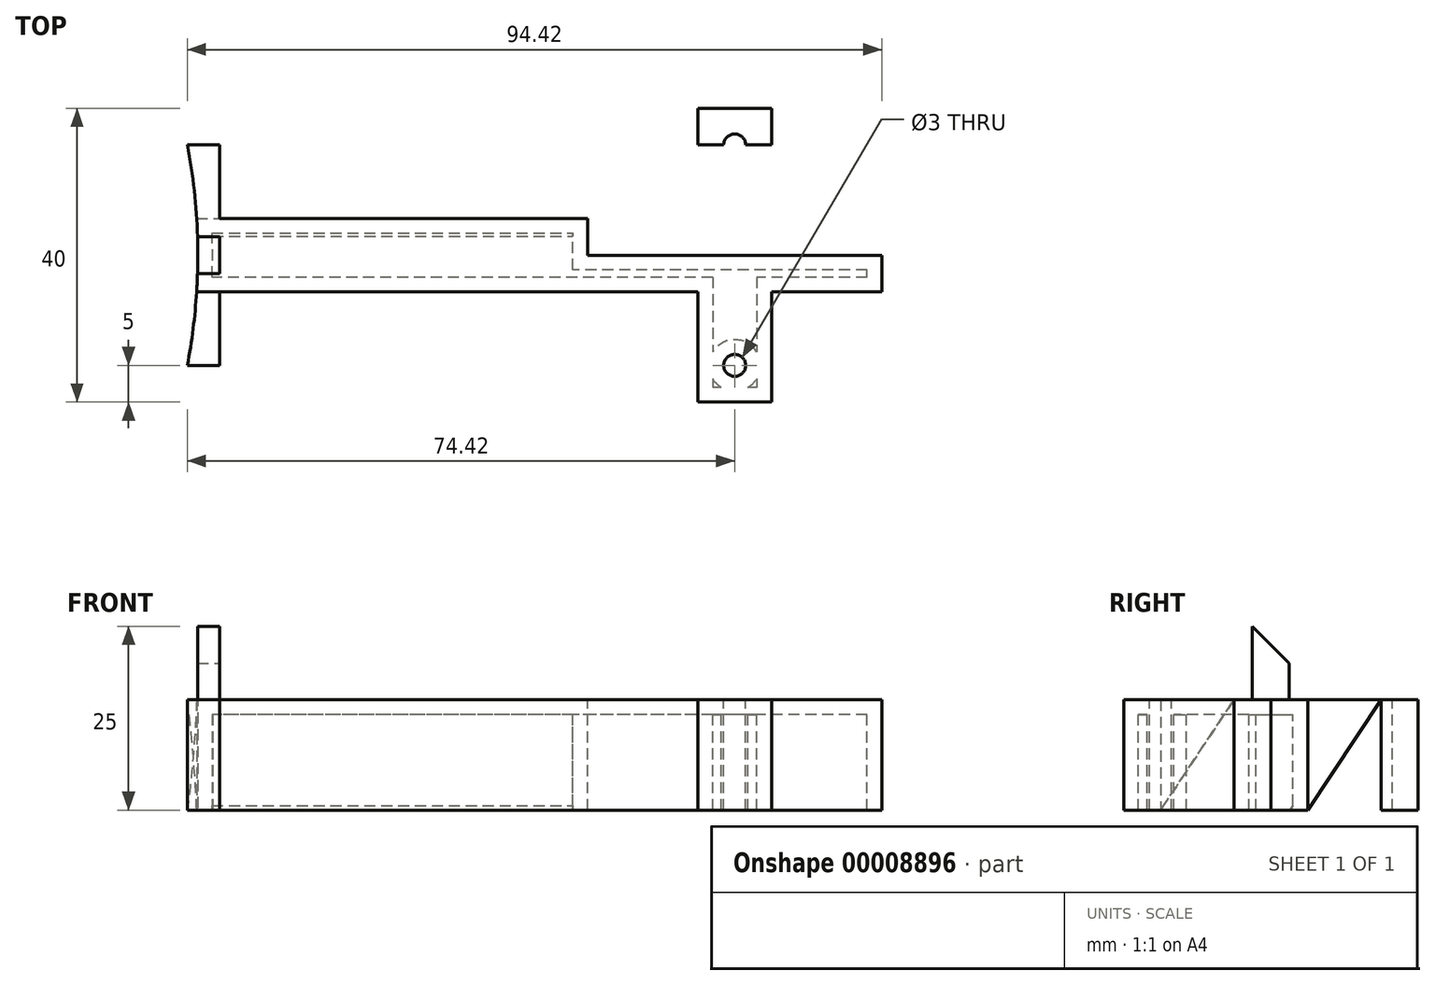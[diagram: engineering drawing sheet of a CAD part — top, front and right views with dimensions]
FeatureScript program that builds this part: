
annotation { "Feature Type Name" : "Feature", "Feature Type Description" : "" }
export const myFeature = defineFeature(function(context is Context, id is Id, definition is map)
    precondition{}
    {
        {
            var Q0;
            Q0=qCreatedBy(makeId("Top.planeOp"),FACE);
            var sketch = newSketch(context, id + "F0", { "sketchPlane" : qUnion([Q0])});
            skArc(sketch, "E0", {"start": v(78.58, -15) * mm, "mid": v(80, 0) * mm, "end": v(78.58, 15) * mm});
            skArc(sketch, "E1.0", {"start": v(81.63, -15) * mm, "mid": v(83, 0) * mm, "end": v(81.63, 15) * mm});
            skLineSegment(sketch, "E2", {"start": v(80, 0) * mm, "end": v(83, 0) * mm, "construction": true});
            skLineSegment(sketch, "E3.0", {"start": v(79.84, -5) * mm, "end": v(83, -5) * mm, "construction": true});
            skLineSegment(sketch, "E4.0", {"start": v(79.84, 5) * mm, "end": v(83, 5) * mm, "construction": true});
            skLineSegment(sketch, "E5", {"start": v(83, 0) * mm, "end": v(83, 15) * mm});
            skLineSegment(sketch, "E6", {"start": v(83, 0) * mm, "end": v(83, -15) * mm});
            skLineSegment(sketch, "E7", {"start": v(83, 15) * mm, "end": v(78.58, 15) * mm});
            skLineSegment(sketch, "E8", {"start": v(83, -15) * mm, "end": v(78.58, -15) * mm});
            skSolve(sketch);
        }
        {
            var Q0;
            {var subQ3=sQuery(id+"F0.wireOp",EDGE,"E0");Q0=makeQuery(id+"F0.imprint","IMPRINT",FACE,{"disambiguationData":[TD([[makeQuery(id+"F0.imprint","IMPRINT",EDGE,{"derivedFrom":subQ3}),-1.0]])]});}
            var Q1;
            {var subQ1=sQuery(id+"F0.wireOp",EDGE,"E5");Q1=makeQuery(id+"F0.imprint","IMPRINT",FACE,{"disambiguationData":[TD([[makeQuery(id+"F0.imprint","IMPRINT",EDGE,{"derivedFrom":subQ1}),1.0]])]});}
            var Q2;
            {var subQ1=sQuery(id+"F0.wireOp",EDGE,"E6");Q2=makeQuery(id+"F0.imprint","IMPRINT",FACE,{"disambiguationData":[TD([[makeQuery(id+"F0.imprint","IMPRINT",EDGE,{"derivedFrom":subQ1}),-1.0]])]});}
            extrude(context, id + "F1", {"entities" : qUnion([Q0, Q1, Q2]), "depth" : 15 * mm});
        }
        {
            var Q0;
            Q0=makeQuery(id+"F1.opExtrude","SWEPT_FACE",FACE,{"disambiguationData":[OSD([sQuery(id+"F0.wireOp",EDGE,"E5"),sQuery(id+"F0.wireOp",EDGE,"E6")])]});
            var sketch = newSketch(context, id + "F2", { "sketchPlane" : qUnion([Q0])});
            skLineSegment(sketch, "E9.0", {"start": v(-15, 10) * mm, "end": v(15, 10) * mm});
            skLineSegment(sketch, "E10", {"start": v(0, 10) * mm, "end": v(0, 15) * mm});
            skLineSegment(sketch, "E11.0", {"start": v(5, 0) * mm, "end": v(5, 15) * mm});
            skLineSegment(sketch, "E12.0", {"start": v(-5, 0) * mm, "end": v(-5, 15) * mm});
            skLineSegment(sketch, "E13", {"start": v(15, 0) * mm, "end": v(-15, 0) * mm});
            skLineSegment(sketch, "E14", {"start": v(15, 15) * mm, "end": v(-15, 15) * mm});
            skSolve(sketch);
        }
        {
            var Q0;
            {var subQ2=sQuery(id+"F2.wireOp",EDGE,"E10");Q0=makeQuery(id+"F2.imprint","IMPRINT",FACE,{"disambiguationData":[TD([[makeQuery(id+"F2.imprint","IMPRINT",EDGE,{"derivedFrom":subQ2}),-1.0]])]});}
            var Q1;
            {var subQ2=sQuery(id+"F2.wireOp",EDGE,"E10");Q1=makeQuery(id+"F2.imprint","IMPRINT",FACE,{"disambiguationData":[TD([[makeQuery(id+"F2.imprint","IMPRINT",EDGE,{"derivedFrom":subQ2}),1.0]])]});}
            var Q2;
            {var subQ5=sQuery(id+"F2.wireOp",EDGE,"E9.0");var subQ8=makeQuery(id+"F2.imprint","INTERSECT",VERTEX,{"derivedFrom":[subQ5,sQuery(id+"F2.wireOp",EDGE,"E10")]});Q2=makeQuery(id+"F2.imprint","IMPRINT",FACE,{"disambiguationData":[TD([[makeQuery(id+"F2.imprint","IMPRINT",EDGE,{"disambiguationData":[TD([[subQ8,1.0]])],"derivedFrom":subQ5}),-1.0]])]});}
            extrude(context, id + "F3", {"entities" : qUnion([Q0, Q1, Q2]), "operationType" : NewBodyOperationType.ADD, "depth" : 90 * mm});
        }
        {
            var Q0;
            Q0=makeQuery(id+"F3.boolean.opBoolean","MERGE",FACE,{"derivedFrom":[makeQuery(id+"F1.opExtrude","CAP_FACE",FACE,{"disambiguationData":[OSD([sQuery(id+"F0.wireOp",EDGE,"E0"),sQuery(id+"F0.wireOp",EDGE,"E5"),sQuery(id+"F0.wireOp",EDGE,"E6"),sQuery(id+"F0.wireOp",EDGE,"E7"),sQuery(id+"F0.wireOp",EDGE,"E8")])],"isStart":false}),makeQuery(id+"F3.opExtrude","SWEPT_FACE",FACE,{"disambiguationData":[OSD([sQuery(id+"F2.wireOp",EDGE,"E14")])]})]});
            var sketch = newSketch(context, id + "F4", { "sketchPlane" : qUnion([Q0])});
            skLineSegment(sketch, "E15.0", {"start": v(133, -5) * mm, "end": v(133, 5) * mm});
            skLineSegment(sketch, "E16.0", {"start": v(138, -5) * mm, "end": v(138, 5) * mm});
            skLineSegment(sketch, "E17.0", {"start": v(168, -5) * mm, "end": v(168, 5) * mm});
            skLineSegment(sketch, "E18", {"start": v(168, -5) * mm, "end": v(133, -5) * mm});
            skLineSegment(sketch, "E19.0", {"start": v(173, 0) * mm, "end": v(83, 0) * mm});
            skCircle(sketch, "E20", {"center": v(168, 0) * mm, "radius": 1.5 * mm});
            skCircle(sketch, "E21", {"center": v(138, 0) * mm, "radius": 1.5 * mm});
            skSolve(sketch);
        }
        {
            var Q0;
            {var subQ0=sQuery(id+"F4.wireOp",EDGE,"E20");var subQ3=sQuery(id+"F4.wireOp",EDGE,"E17.0");var subQ4=makeQuery(id+"F4.imprint","INTERSECT",VERTEX,{"disambiguationData":[OD(0.0)],"derivedFrom":[subQ3,subQ0]});Q0=makeQuery(id+"F4.imprint","IMPRINT",FACE,{"disambiguationData":[TD([[makeQuery(id+"F4.imprint","IMPRINT",EDGE,{"disambiguationData":[TD([[subQ4,-1.0]])],"derivedFrom":subQ3}),1.0]])]});}
            var Q1;
            {var subQ0=sQuery(id+"F4.wireOp",EDGE,"E20");var subQ3=sQuery(id+"F4.wireOp",EDGE,"E17.0");var subQ4=makeQuery(id+"F4.imprint","INTERSECT",VERTEX,{"disambiguationData":[OD(0.0)],"derivedFrom":[subQ3,subQ0]});Q1=makeQuery(id+"F4.imprint","IMPRINT",FACE,{"disambiguationData":[TD([[makeQuery(id+"F4.imprint","IMPRINT",EDGE,{"disambiguationData":[TD([[subQ4,-1.0]])],"derivedFrom":subQ3}),-1.0]])]});}
            var Q2;
            {var subQ1=sQuery(id+"F4.wireOp",EDGE,"E19.0");var subQ3=sQuery(id+"F4.wireOp",EDGE,"E17.0");var subQ5=makeQuery(id+"F4.imprint","INTERSECT",VERTEX,{"derivedFrom":[subQ3,subQ1]});Q2=makeQuery(id+"F4.imprint","IMPRINT",FACE,{"disambiguationData":[TD([[makeQuery(id+"F4.imprint","IMPRINT",EDGE,{"disambiguationData":[TD([[subQ5,-1.0]])],"derivedFrom":subQ3}),1.0]])]});}
            var Q3;
            {var subQ1=sQuery(id+"F4.wireOp",EDGE,"E19.0");var subQ3=sQuery(id+"F4.wireOp",EDGE,"E17.0");var subQ5=makeQuery(id+"F4.imprint","INTERSECT",VERTEX,{"derivedFrom":[subQ3,subQ1]});Q3=makeQuery(id+"F4.imprint","IMPRINT",FACE,{"disambiguationData":[TD([[makeQuery(id+"F4.imprint","IMPRINT",EDGE,{"disambiguationData":[TD([[subQ5,-1.0]])],"derivedFrom":subQ3}),-1.0]])]});}
            var Q4;
            {var subQ0=sQuery(id+"F4.wireOp",EDGE,"E21");var subQ3=sQuery(id+"F4.wireOp",EDGE,"E16.0");var subQ4=makeQuery(id+"F4.imprint","INTERSECT",VERTEX,{"disambiguationData":[OD(0.0)],"derivedFrom":[subQ3,subQ0]});Q4=makeQuery(id+"F4.imprint","IMPRINT",FACE,{"disambiguationData":[TD([[makeQuery(id+"F4.imprint","IMPRINT",EDGE,{"disambiguationData":[TD([[subQ4,-1.0]])],"derivedFrom":subQ3}),1.0]])]});}
            var Q5;
            {var subQ1=sQuery(id+"F4.wireOp",EDGE,"E19.0");var subQ3=sQuery(id+"F4.wireOp",EDGE,"E16.0");var subQ5=makeQuery(id+"F4.imprint","INTERSECT",VERTEX,{"derivedFrom":[subQ3,subQ1]});Q5=makeQuery(id+"F4.imprint","IMPRINT",FACE,{"disambiguationData":[TD([[makeQuery(id+"F4.imprint","IMPRINT",EDGE,{"disambiguationData":[TD([[subQ5,-1.0]])],"derivedFrom":subQ3}),1.0]])]});}
            var Q6;
            {var subQ1=sQuery(id+"F4.wireOp",EDGE,"E19.0");var subQ3=sQuery(id+"F4.wireOp",EDGE,"E16.0");var subQ5=makeQuery(id+"F4.imprint","INTERSECT",VERTEX,{"derivedFrom":[subQ3,subQ1]});Q6=makeQuery(id+"F4.imprint","IMPRINT",FACE,{"disambiguationData":[TD([[makeQuery(id+"F4.imprint","IMPRINT",EDGE,{"disambiguationData":[TD([[subQ5,-1.0]])],"derivedFrom":subQ3}),-1.0]])]});}
            var Q7;
            {var subQ1=sQuery(id+"F4.wireOp",EDGE,"E21");var subQ3=sQuery(id+"F4.wireOp",EDGE,"E16.0");var subQ5=makeQuery(id+"F4.imprint","INTERSECT",VERTEX,{"disambiguationData":[OD(0.0)],"derivedFrom":[subQ3,subQ1]});Q7=makeQuery(id+"F4.imprint","IMPRINT",FACE,{"disambiguationData":[TD([[makeQuery(id+"F4.imprint","IMPRINT",EDGE,{"disambiguationData":[TD([[subQ5,-1.0]])],"derivedFrom":subQ3}),-1.0]])]});}
            extrude(context, id + "F5", {"entities" : qUnion([Q0, Q1, Q2, Q3, Q4, Q5, Q6, Q7]), "operationType" : NewBodyOperationType.REMOVE, "oppositeDirection" : true, "depth" : 25 * mm});
        }
        {
            var Q0;
            Q0=makeQuery(id+"F3.boolean.opBoolean","MERGE",FACE,{"derivedFrom":[makeQuery(id+"F1.opExtrude","CAP_FACE",FACE,{"disambiguationData":[OSD([sQuery(id+"F0.wireOp",EDGE,"E0"),sQuery(id+"F0.wireOp",EDGE,"E5"),sQuery(id+"F0.wireOp",EDGE,"E6"),sQuery(id+"F0.wireOp",EDGE,"E7"),sQuery(id+"F0.wireOp",EDGE,"E8")])],"isStart":false}),makeQuery(id+"F3.opExtrude","SWEPT_FACE",FACE,{"disambiguationData":[OSD([sQuery(id+"F2.wireOp",EDGE,"E14")])]})]});
            var sketch = newSketch(context, id + "F6", { "sketchPlane" : qUnion([Q0])});
            skLineSegment(sketch, "E22.0", {"start": v(153, -5) * mm, "end": v(153, 5) * mm});
            skLineSegment(sketch, "E23", {"start": v(153, 5) * mm, "end": v(153, 20) * mm});
            skLineSegment(sketch, "E24", {"start": v(153, -5) * mm, "end": v(153, -20) * mm});
            skLineSegment(sketch, "E25.0", {"start": v(158, 5) * mm, "end": v(158, 20) * mm});
            skLineSegment(sketch, "E26.0", {"start": v(148, 5) * mm, "end": v(148, 20) * mm});
            skLineSegment(sketch, "E27.0", {"start": v(148, -5) * mm, "end": v(148, -20) * mm});
            skLineSegment(sketch, "E28.0", {"start": v(158, -5) * mm, "end": v(158, -20) * mm});
            skLineSegment(sketch, "E29", {"start": v(158, -20) * mm, "end": v(148, -20) * mm});
            skLineSegment(sketch, "E30", {"start": v(158, 20) * mm, "end": v(148, 20) * mm});
            skLineSegment(sketch, "E31.0", {"start": v(158, 15) * mm, "end": v(148, 15) * mm});
            skLineSegment(sketch, "E32.0", {"start": v(158, -15) * mm, "end": v(148, -15) * mm});
            skCircle(sketch, "E33", {"center": v(153, -15) * mm, "radius": 1.5 * mm});
            skCircle(sketch, "E34", {"center": v(153, 15) * mm, "radius": 1.5 * mm});
            skSolve(sketch);
        }
        {
            var Q0;
            {var subQ5=sQuery(id+"F6.wireOp",EDGE,"E23");var subQ7=sQuery(id+"F6.wireOp",EDGE,"E30");var subQ9=makeQuery(id+"F6.imprint","INTERSECT",VERTEX,{"derivedFrom":[subQ5,subQ7]});Q0=makeQuery(id+"F6.imprint","IMPRINT",FACE,{"disambiguationData":[TD([[makeQuery(id+"F6.imprint","IMPRINT",EDGE,{"disambiguationData":[TD([[subQ9,1.0]])],"derivedFrom":subQ5}),-1.0]])]});}
            var Q1;
            {var subQ3=sQuery(id+"F6.wireOp",EDGE,"E23");var subQ7=sQuery(id+"F6.wireOp",EDGE,"E30");var subQ9=makeQuery(id+"F6.imprint","INTERSECT",VERTEX,{"derivedFrom":[subQ3,subQ7]});Q1=makeQuery(id+"F6.imprint","IMPRINT",FACE,{"disambiguationData":[TD([[makeQuery(id+"F6.imprint","IMPRINT",EDGE,{"disambiguationData":[TD([[subQ9,1.0]])],"derivedFrom":subQ3}),1.0]])]});}
            var Q2;
            {var subQ1=sQuery(id+"F6.wireOp",EDGE,"E26.0");var subQ6=sQuery(id+"F6.wireOp",EDGE,"E31.0");var subQ9=makeQuery(id+"F6.imprint","INTERSECT",VERTEX,{"derivedFrom":[subQ1,subQ6]});Q2=makeQuery(id+"F6.imprint","IMPRINT",FACE,{"disambiguationData":[TD([[makeQuery(id+"F6.imprint","IMPRINT",EDGE,{"disambiguationData":[TD([[subQ9,1.0]])],"derivedFrom":subQ6}),1.0]])]});}
            var Q3;
            {var subQ1=sQuery(id+"F6.wireOp",EDGE,"E25.0");var subQ6=sQuery(id+"F6.wireOp",EDGE,"E31.0");var subQ9=makeQuery(id+"F6.imprint","INTERSECT",VERTEX,{"derivedFrom":[subQ1,subQ6]});Q3=makeQuery(id+"F6.imprint","IMPRINT",FACE,{"disambiguationData":[TD([[makeQuery(id+"F6.imprint","IMPRINT",EDGE,{"disambiguationData":[TD([[subQ9,-1.0]])],"derivedFrom":subQ6}),1.0]])]});}
            var Q4;
            {var subQ1=sQuery(id+"F6.wireOp",EDGE,"E28.0");var subQ6=sQuery(id+"F6.wireOp",EDGE,"E32.0");var subQ9=makeQuery(id+"F6.imprint","INTERSECT",VERTEX,{"derivedFrom":[subQ1,subQ6]});Q4=makeQuery(id+"F6.imprint","IMPRINT",FACE,{"disambiguationData":[TD([[makeQuery(id+"F6.imprint","IMPRINT",EDGE,{"disambiguationData":[TD([[subQ9,-1.0]])],"derivedFrom":subQ6}),-1.0]])]});}
            var Q5;
            {var subQ3=sQuery(id+"F6.wireOp",EDGE,"E24");var subQ7=sQuery(id+"F6.wireOp",EDGE,"E29");var subQ9=makeQuery(id+"F6.imprint","INTERSECT",VERTEX,{"derivedFrom":[subQ3,subQ7]});Q5=makeQuery(id+"F6.imprint","IMPRINT",FACE,{"disambiguationData":[TD([[makeQuery(id+"F6.imprint","IMPRINT",EDGE,{"disambiguationData":[TD([[subQ9,1.0]])],"derivedFrom":subQ3}),1.0]])]});}
            var Q6;
            {var subQ3=sQuery(id+"F6.wireOp",EDGE,"E24");var subQ7=sQuery(id+"F6.wireOp",EDGE,"E29");var subQ9=makeQuery(id+"F6.imprint","INTERSECT",VERTEX,{"derivedFrom":[subQ3,subQ7]});Q6=makeQuery(id+"F6.imprint","IMPRINT",FACE,{"disambiguationData":[TD([[makeQuery(id+"F6.imprint","IMPRINT",EDGE,{"disambiguationData":[TD([[subQ9,1.0]])],"derivedFrom":subQ3}),-1.0]])]});}
            var Q7;
            {var subQ1=sQuery(id+"F6.wireOp",EDGE,"E27.0");var subQ6=sQuery(id+"F6.wireOp",EDGE,"E32.0");var subQ9=makeQuery(id+"F6.imprint","INTERSECT",VERTEX,{"derivedFrom":[subQ1,subQ6]});Q7=makeQuery(id+"F6.imprint","IMPRINT",FACE,{"disambiguationData":[TD([[makeQuery(id+"F6.imprint","IMPRINT",EDGE,{"disambiguationData":[TD([[subQ9,1.0]])],"derivedFrom":subQ6}),-1.0]])]});}
            extrude(context, id + "F7", {"entities" : qUnion([Q0, Q1, Q2, Q3, Q4, Q5, Q6, Q7]), "operationType" : NewBodyOperationType.ADD, "oppositeDirection" : true, "depth" : 15 * mm});
        }
        {
            var Q0;
            {var subQ0=sQuery(id+"F0.wireOp",EDGE,"E5");var subQ1=sQuery(id+"F0.wireOp",EDGE,"E6");var subQ2=sQuery(id+"F0.wireOp",EDGE,"E8");Q0=makeQuery(id+"F3.boolean.opBoolean","SPLIT",FACE,{"disambiguationData":[TD([makeQuery(id+"F1.opExtrude","SWEPT_FACE",FACE,{"disambiguationData":[OSD([subQ2])]})])],"derivedFrom":makeQuery(id+"F1.opExtrude","SWEPT_FACE",FACE,{"disambiguationData":[OSD([subQ0,subQ1])]})});}
            var sketch = newSketch(context, id + "F8", { "sketchPlane" : qUnion([Q0])});
            skLineSegment(sketch, "E35", {"start": v(-15, 15) * mm, "end": v(-5, 0) * mm});
            skLineSegment(sketch, "E36", {"start": v(-15, 0) * mm, "end": v(-5, 15) * mm});
            skCircle(sketch, "E37", {"center": v(-10, 7.5) * mm, "radius": 1.5 * mm});
            skSolve(sketch);
        }
        {
            var Q0;
            {var subQ0=sQuery(id+"F0.wireOp",EDGE,"E5");var subQ1=sQuery(id+"F0.wireOp",EDGE,"E6");var subQ2=sQuery(id+"F0.wireOp",EDGE,"E7");Q0=makeQuery(id+"F3.boolean.opBoolean","SPLIT",FACE,{"disambiguationData":[TD([makeQuery(id+"F1.opExtrude","SWEPT_FACE",FACE,{"disambiguationData":[OSD([subQ2])]})])],"derivedFrom":makeQuery(id+"F1.opExtrude","SWEPT_FACE",FACE,{"disambiguationData":[OSD([subQ0,subQ1])]})});}
            var sketch = newSketch(context, id + "F9", { "sketchPlane" : qUnion([Q0])});
            skLineSegment(sketch, "E38", {"start": v(5, 15) * mm, "end": v(15, 0) * mm});
            skLineSegment(sketch, "E39", {"start": v(15, 15) * mm, "end": v(5, 0) * mm});
            skCircle(sketch, "E40", {"center": v(10, 7.5) * mm, "radius": 1.5 * mm});
            skSolve(sketch);
        }
        {
            var Q0;
            {var subQ1=sQuery(id+"F8.wireOp",EDGE,"E36");var subQ3=sQuery(id+"F8.wireOp",EDGE,"E35");var subQ5=makeQuery(id+"F8.imprint","INTERSECT",VERTEX,{"derivedFrom":[subQ3,subQ1]});Q0=makeQuery(id+"F8.imprint","IMPRINT",FACE,{"disambiguationData":[TD([[makeQuery(id+"F8.imprint","IMPRINT",EDGE,{"disambiguationData":[TD([[subQ5,-1.0]])],"derivedFrom":subQ3}),1.0]])]});}
            var Q1;
            {var subQ0=sQuery(id+"F8.wireOp",EDGE,"E37");var subQ3=sQuery(id+"F8.wireOp",EDGE,"E35");var subQ4=makeQuery(id+"F8.imprint","INTERSECT",VERTEX,{"disambiguationData":[OD(0.0)],"derivedFrom":[subQ3,subQ0]});Q1=makeQuery(id+"F8.imprint","IMPRINT",FACE,{"disambiguationData":[TD([[makeQuery(id+"F8.imprint","IMPRINT",EDGE,{"disambiguationData":[TD([[subQ4,-1.0]])],"derivedFrom":subQ3}),1.0]])]});}
            var Q2;
            {var subQ0=sQuery(id+"F8.wireOp",EDGE,"E37");var subQ3=sQuery(id+"F8.wireOp",EDGE,"E35");var subQ4=makeQuery(id+"F8.imprint","INTERSECT",VERTEX,{"disambiguationData":[OD(0.0)],"derivedFrom":[subQ3,subQ0]});Q2=makeQuery(id+"F8.imprint","IMPRINT",FACE,{"disambiguationData":[TD([[makeQuery(id+"F8.imprint","IMPRINT",EDGE,{"disambiguationData":[TD([[subQ4,-1.0]])],"derivedFrom":subQ3}),-1.0]])]});}
            var Q3;
            {var subQ1=sQuery(id+"F8.wireOp",EDGE,"E36");var subQ3=sQuery(id+"F8.wireOp",EDGE,"E35");var subQ5=makeQuery(id+"F8.imprint","INTERSECT",VERTEX,{"derivedFrom":[subQ3,subQ1]});Q3=makeQuery(id+"F8.imprint","IMPRINT",FACE,{"disambiguationData":[TD([[makeQuery(id+"F8.imprint","IMPRINT",EDGE,{"disambiguationData":[TD([[subQ5,-1.0]])],"derivedFrom":subQ3}),-1.0]])]});}
            var Q4;
            {var subQ1=sQuery(id+"F9.wireOp",EDGE,"E39");var subQ3=sQuery(id+"F9.wireOp",EDGE,"E38");var subQ5=makeQuery(id+"F9.imprint","INTERSECT",VERTEX,{"derivedFrom":[subQ3,subQ1]});Q4=makeQuery(id+"F9.imprint","IMPRINT",FACE,{"disambiguationData":[TD([[makeQuery(id+"F9.imprint","IMPRINT",EDGE,{"disambiguationData":[TD([[subQ5,-1.0]])],"derivedFrom":subQ3}),-1.0]])]});}
            var Q5;
            {var subQ0=sQuery(id+"F9.wireOp",EDGE,"E40");var subQ3=sQuery(id+"F9.wireOp",EDGE,"E38");var subQ4=makeQuery(id+"F9.imprint","INTERSECT",VERTEX,{"disambiguationData":[OD(0.0)],"derivedFrom":[subQ3,subQ0]});Q5=makeQuery(id+"F9.imprint","IMPRINT",FACE,{"disambiguationData":[TD([[makeQuery(id+"F9.imprint","IMPRINT",EDGE,{"disambiguationData":[TD([[subQ4,-1.0]])],"derivedFrom":subQ3}),-1.0]])]});}
            var Q6;
            {var subQ0=sQuery(id+"F9.wireOp",EDGE,"E40");var subQ3=sQuery(id+"F9.wireOp",EDGE,"E38");var subQ4=makeQuery(id+"F9.imprint","INTERSECT",VERTEX,{"disambiguationData":[OD(0.0)],"derivedFrom":[subQ3,subQ0]});Q6=makeQuery(id+"F9.imprint","IMPRINT",FACE,{"disambiguationData":[TD([[makeQuery(id+"F9.imprint","IMPRINT",EDGE,{"disambiguationData":[TD([[subQ4,-1.0]])],"derivedFrom":subQ3}),1.0]])]});}
            var Q7;
            {var subQ1=sQuery(id+"F9.wireOp",EDGE,"E39");var subQ3=sQuery(id+"F9.wireOp",EDGE,"E38");var subQ5=makeQuery(id+"F9.imprint","INTERSECT",VERTEX,{"derivedFrom":[subQ3,subQ1]});Q7=makeQuery(id+"F9.imprint","IMPRINT",FACE,{"disambiguationData":[TD([[makeQuery(id+"F9.imprint","IMPRINT",EDGE,{"disambiguationData":[TD([[subQ5,-1.0]])],"derivedFrom":subQ3}),1.0]])]});}
            extrude(context, id + "F10", {"entities" : qUnion([Q0, Q1, Q2, Q3, Q4, Q5, Q6, Q7]), "operationType" : NewBodyOperationType.REMOVE, "oppositeDirection" : true, "depth" : 25 * mm});
        }
        {
            var Q0;
            {var subQ0=sQuery(id+"F2.wireOp",EDGE,"E14");Q0=makeQuery(id+"F7.boolean.opBoolean","MERGE",FACE,{"derivedFrom":[makeQuery(id+"F3.boolean.opBoolean","MERGE",FACE,{"derivedFrom":[makeQuery(id+"F1.opExtrude","CAP_FACE",FACE,{"disambiguationData":[OSD([sQuery(id+"F0.wireOp",EDGE,"E0"),sQuery(id+"F0.wireOp",EDGE,"E5"),sQuery(id+"F0.wireOp",EDGE,"E6"),sQuery(id+"F0.wireOp",EDGE,"E7"),sQuery(id+"F0.wireOp",EDGE,"E8")])],"isStart":false}),makeQuery(id+"F3.opExtrude","SWEPT_FACE",FACE,{"disambiguationData":[OSD([subQ0])]})]}),makeQuery(id+"F7.opExtrude","CAP_FACE",FACE,{"disambiguationData":[OSD([sQuery(id+"F2.wireOp",EDGE,"E11.0"),subQ0,sQuery(id+"F6.wireOp",EDGE,"E25.0"),sQuery(id+"F6.wireOp",EDGE,"E26.0"),sQuery(id+"F6.wireOp",EDGE,"E30"),sQuery(id+"F6.wireOp",EDGE,"E34")])],"isStart":true}),makeQuery(id+"F7.opExtrude","CAP_FACE",FACE,{"disambiguationData":[OSD([sQuery(id+"F2.wireOp",EDGE,"E12.0"),subQ0,sQuery(id+"F6.wireOp",EDGE,"E27.0"),sQuery(id+"F6.wireOp",EDGE,"E28.0"),sQuery(id+"F6.wireOp",EDGE,"E29"),sQuery(id+"F6.wireOp",EDGE,"E33")])],"isStart":true})]});}
            var sketch = newSketch(context, id + "F11", { "sketchPlane" : qUnion([Q0])});
            skLineSegment(sketch, "E41", {"start": v(0, 0) * mm, "end": v(89.68, 0) * mm});
            skLineSegment(sketch, "E42.0", {"start": v(83, 0) * mm, "end": v(83, -2.5) * mm});
            skLineSegment(sketch, "E43.0", {"start": v(83, 0) * mm, "end": v(83, 2.5) * mm});
            skLineSegment(sketch, "E44", {"start": v(83, 2.5) * mm, "end": v(79.96, 2.5) * mm});
            skLineSegment(sketch, "E45", {"start": v(83, -2.5) * mm, "end": v(79.96, -2.5) * mm});
            skArc(sketch, "E46.0", {"start": v(78.58, -15) * mm, "mid": v(80, 0) * mm, "end": v(78.58, 15) * mm});
            skSolve(sketch);
        }
        {
            var Q0;
            {var subQ4=sQuery(id+"F11.wireOp",EDGE,"E43.0");Q0=makeQuery(id+"F11.imprint","IMPRINT",FACE,{"disambiguationData":[TD([[makeQuery(id+"F11.imprint","IMPRINT",EDGE,{"derivedFrom":subQ4}),1.0]])]});}
            var Q1;
            {var subQ4=sQuery(id+"F11.wireOp",EDGE,"E42.0");Q1=makeQuery(id+"F11.imprint","IMPRINT",FACE,{"disambiguationData":[TD([[makeQuery(id+"F11.imprint","IMPRINT",EDGE,{"derivedFrom":subQ4}),-1.0]])]});}
            extrude(context, id + "F12", {"entities" : qUnion([Q0, Q1]), "operationType" : NewBodyOperationType.ADD, "depth" : 10 * mm});
        }
        {
            var Q0;
            Q0=makeQuery(id+"F12.opExtrude","SWEPT_FACE",FACE,{"disambiguationData":[OSD([sQuery(id+"F11.wireOp",EDGE,"E42.0"),sQuery(id+"F11.wireOp",EDGE,"E43.0")])]});
            var sketch = newSketch(context, id + "F13", { "sketchPlane" : qUnion([Q0])});
            skLineSegment(sketch, "E47.0", {"start": v(-2.5, 20) * mm, "end": v(2.5, 20) * mm});
            skLineSegment(sketch, "E48", {"start": v(-2.5, 20) * mm, "end": v(2.5, 25) * mm});
            skLineSegment(sketch, "E49", {"start": v(2.5, 20) * mm, "end": v(-2.5, 25) * mm});
            skCircle(sketch, "E50", {"center": v(0, 22.5) * mm, "radius": 1.5 * mm});
            skSolve(sketch);
        }
        {
            var Q0;
            {var subQ1=sQuery(id+"F13.wireOp",EDGE,"E49");var subQ3=sQuery(id+"F13.wireOp",EDGE,"E48");var subQ5=makeQuery(id+"F13.imprint","INTERSECT",VERTEX,{"derivedFrom":[subQ3,subQ1]});Q0=makeQuery(id+"F13.imprint","IMPRINT",FACE,{"disambiguationData":[TD([[makeQuery(id+"F13.imprint","IMPRINT",EDGE,{"disambiguationData":[TD([[subQ5,-1.0]])],"derivedFrom":subQ3}),1.0]])]});}
            var Q1;
            {var subQ0=sQuery(id+"F13.wireOp",EDGE,"E50");var subQ3=sQuery(id+"F13.wireOp",EDGE,"E48");var subQ4=makeQuery(id+"F13.imprint","INTERSECT",VERTEX,{"disambiguationData":[OD(0.0)],"derivedFrom":[subQ3,subQ0]});Q1=makeQuery(id+"F13.imprint","IMPRINT",FACE,{"disambiguationData":[TD([[makeQuery(id+"F13.imprint","IMPRINT",EDGE,{"disambiguationData":[TD([[subQ4,-1.0]])],"derivedFrom":subQ3}),1.0]])]});}
            var Q2;
            {var subQ1=sQuery(id+"F13.wireOp",EDGE,"E49");var subQ3=sQuery(id+"F13.wireOp",EDGE,"E48");var subQ5=makeQuery(id+"F13.imprint","INTERSECT",VERTEX,{"derivedFrom":[subQ3,subQ1]});Q2=makeQuery(id+"F13.imprint","IMPRINT",FACE,{"disambiguationData":[TD([[makeQuery(id+"F13.imprint","IMPRINT",EDGE,{"disambiguationData":[TD([[subQ5,-1.0]])],"derivedFrom":subQ3}),-1.0]])]});}
            var Q3;
            {var subQ0=sQuery(id+"F13.wireOp",EDGE,"E50");var subQ3=sQuery(id+"F13.wireOp",EDGE,"E48");var subQ4=makeQuery(id+"F13.imprint","INTERSECT",VERTEX,{"disambiguationData":[OD(0.0)],"derivedFrom":[subQ3,subQ0]});Q3=makeQuery(id+"F13.imprint","IMPRINT",FACE,{"disambiguationData":[TD([[makeQuery(id+"F13.imprint","IMPRINT",EDGE,{"disambiguationData":[TD([[subQ4,-1.0]])],"derivedFrom":subQ3}),-1.0]])]});}
            extrude(context, id + "F14", {"entities" : qUnion([Q0, Q1, Q2, Q3]), "operationType" : NewBodyOperationType.REMOVE, "oppositeDirection" : true, "depth" : 25 * mm});
        }
        {
            var Q0;
            {var subQ0=sQuery(id+"F2.wireOp",EDGE,"E14");Q0=makeQuery(id+"F7.boolean.opBoolean","MERGE",FACE,{"derivedFrom":[makeQuery(id+"F3.boolean.opBoolean","MERGE",FACE,{"derivedFrom":[makeQuery(id+"F1.opExtrude","CAP_FACE",FACE,{"disambiguationData":[OSD([sQuery(id+"F0.wireOp",EDGE,"E0"),sQuery(id+"F0.wireOp",EDGE,"E5"),sQuery(id+"F0.wireOp",EDGE,"E6"),sQuery(id+"F0.wireOp",EDGE,"E7"),sQuery(id+"F0.wireOp",EDGE,"E8")])],"isStart":true}),makeQuery(id+"F3.opExtrude","SWEPT_FACE",FACE,{"disambiguationData":[OSD([sQuery(id+"F2.wireOp",EDGE,"E13")])]})]}),makeQuery(id+"F7.opExtrude","CAP_FACE",FACE,{"disambiguationData":[OSD([sQuery(id+"F2.wireOp",EDGE,"E11.0"),subQ0,sQuery(id+"F6.wireOp",EDGE,"E25.0"),sQuery(id+"F6.wireOp",EDGE,"E26.0"),sQuery(id+"F6.wireOp",EDGE,"E30"),sQuery(id+"F6.wireOp",EDGE,"E34")])],"isStart":false}),makeQuery(id+"F7.opExtrude","CAP_FACE",FACE,{"disambiguationData":[OSD([sQuery(id+"F2.wireOp",EDGE,"E12.0"),subQ0,sQuery(id+"F6.wireOp",EDGE,"E27.0"),sQuery(id+"F6.wireOp",EDGE,"E28.0"),sQuery(id+"F6.wireOp",EDGE,"E29"),sQuery(id+"F6.wireOp",EDGE,"E33")])],"isStart":false})]});}
            shell(context, id + "F15", {"entities" : qUnion([Q0]), "thickness" : 2 * mm});
        }
    });
